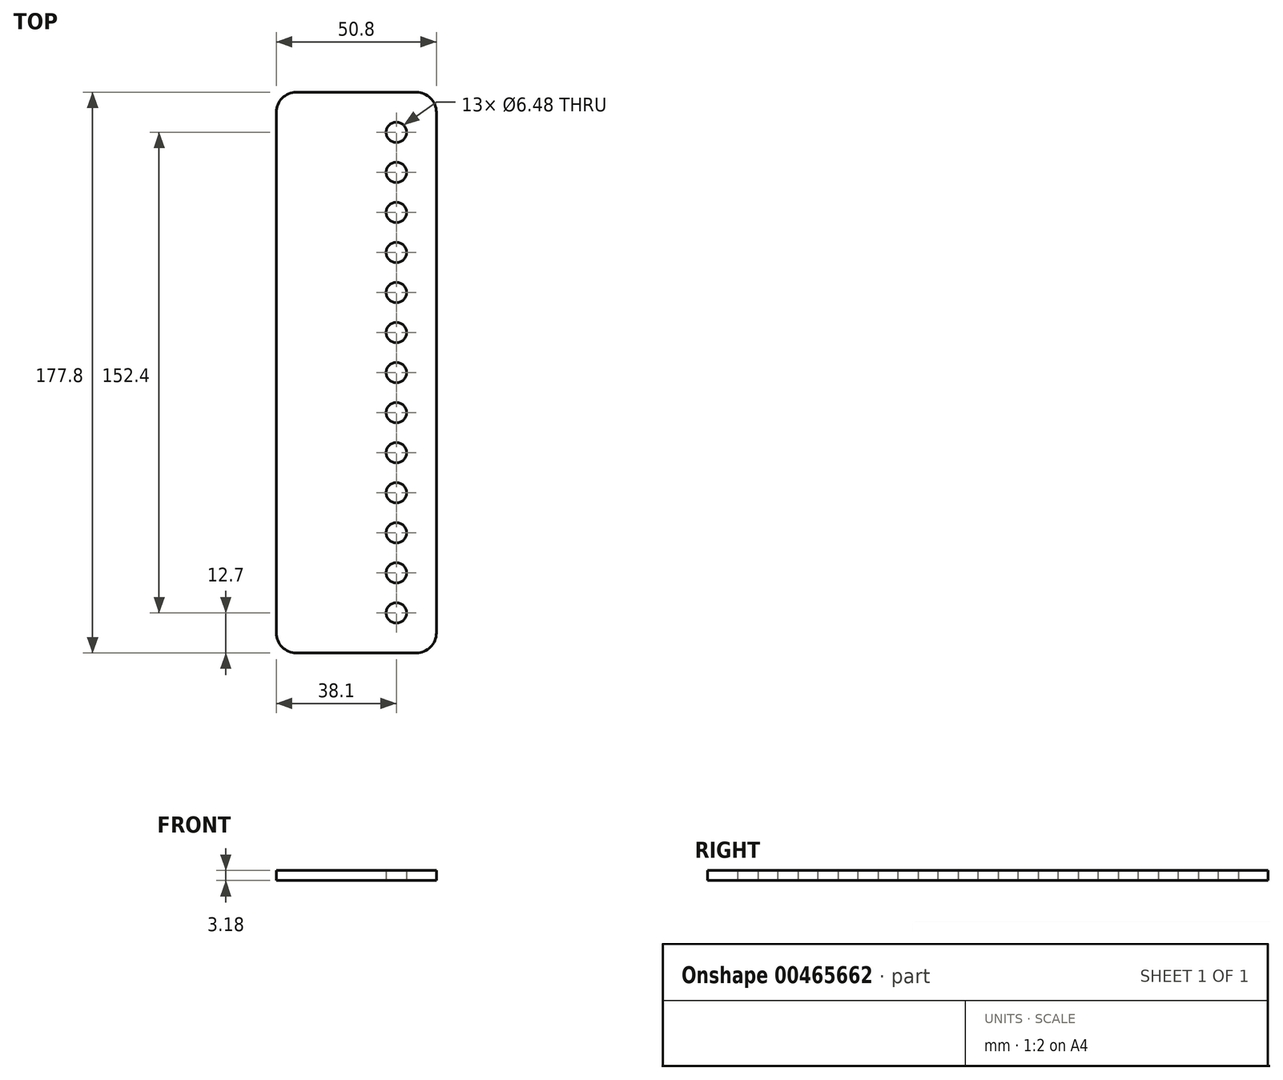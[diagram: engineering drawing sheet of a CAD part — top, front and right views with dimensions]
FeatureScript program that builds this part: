
annotation { "Feature Type Name" : "Feature", "Feature Type Description" : "" }
export const myFeature = defineFeature(function(context is Context, id is Id, definition is map)
    precondition{}
    {
        {
            var Q0;
            Q0=qCreatedBy(makeId("Top.planeOp"),FACE);
            var sketch = newSketch(context, id + "F0", { "sketchPlane" : qUnion([Q0])});
            skLineSegment(sketch, "E0.bottom", {"start": v(6.35, 0) * mm, "end": v(44.45, 0) * mm});
            skLineSegment(sketch, "E0.top", {"start": v(6.35, 177.8) * mm, "end": v(44.45, 177.8) * mm});
            skLineSegment(sketch, "E0.left", {"start": v(0, 6.35) * mm, "end": v(0, 171.45) * mm});
            skLineSegment(sketch, "E0.right", {"start": v(50.8, 6.35) * mm, "end": v(50.8, 171.45) * mm});
            skCircle(sketch, "E1", {"center": v(38.1, 12.7) * mm, "radius": 3.24 * mm});
            skCircle(sketch, "E2.0.1.0", {"center": v(38.1, 25.4) * mm, "radius": 3.24 * mm});
            skCircle(sketch, "E2.0.2.0", {"center": v(38.1, 38.1) * mm, "radius": 3.24 * mm});
            skCircle(sketch, "E2.0.3.0", {"center": v(38.1, 50.8) * mm, "radius": 3.24 * mm});
            skCircle(sketch, "E2.0.4.0", {"center": v(38.1, 63.5) * mm, "radius": 3.24 * mm});
            skCircle(sketch, "E2.0.5.0", {"center": v(38.1, 76.2) * mm, "radius": 3.24 * mm});
            skCircle(sketch, "E2.0.6.0", {"center": v(38.1, 88.9) * mm, "radius": 3.24 * mm});
            skCircle(sketch, "E2.0.7.0", {"center": v(38.1, 101.6) * mm, "radius": 3.24 * mm});
            skCircle(sketch, "E2.0.8.0", {"center": v(38.1, 114.3) * mm, "radius": 3.24 * mm});
            skCircle(sketch, "E2.0.9.0", {"center": v(38.1, 127) * mm, "radius": 3.24 * mm});
            skCircle(sketch, "E2.0.10.0", {"center": v(38.1, 139.7) * mm, "radius": 3.24 * mm});
            skCircle(sketch, "E2.0.11.0", {"center": v(38.1, 152.4) * mm, "radius": 3.24 * mm});
            skCircle(sketch, "E2.0.12.0", {"center": v(38.1, 165.1) * mm, "radius": 3.24 * mm});
            skLineSegment(sketch, "E2.direction1", {"start": v(38.1, 12.7) * mm, "end": v(41.46, 12.7) * mm, "construction": true});
            skLineSegment(sketch, "E2.direction2", {"start": v(38.1, 12.7) * mm, "end": v(38.1, 25.4) * mm, "construction": true});
            skPoint(sketch, "E3.visualSharp", {"position": v(0, 177.8) * mm});
            skArc(sketch, "E3.filletArc", {"start": v(6.35, 177.8) * mm, "mid": v(1.86, 175.94) * mm, "end": v(0, 171.45) * mm});
            skPoint(sketch, "E4.visualSharp", {"position": v(50.8, 177.8) * mm});
            skArc(sketch, "E4.filletArc", {"start": v(50.8, 171.45) * mm, "mid": v(48.94, 175.94) * mm, "end": v(44.45, 177.8) * mm});
            skPoint(sketch, "E5.visualSharp", {"position": v(0, 0) * mm});
            skArc(sketch, "E5.filletArc", {"start": v(0, 6.35) * mm, "mid": v(1.86, 1.86) * mm, "end": v(6.35, 0) * mm});
            skPoint(sketch, "E6.visualSharp", {"position": v(50.8, 0) * mm});
            skArc(sketch, "E6.filletArc", {"start": v(44.45, 0) * mm, "mid": v(48.94, 1.86) * mm, "end": v(50.8, 6.35) * mm});
            skSolve(sketch);
        }
        {
            var Q0;
            Q0=qSketchRegion(id+"F0",true);
            extrude(context, id + "F1", {"entities" : qUnion([Q0]), "depth" : 3.17 * mm});
        }
    });
